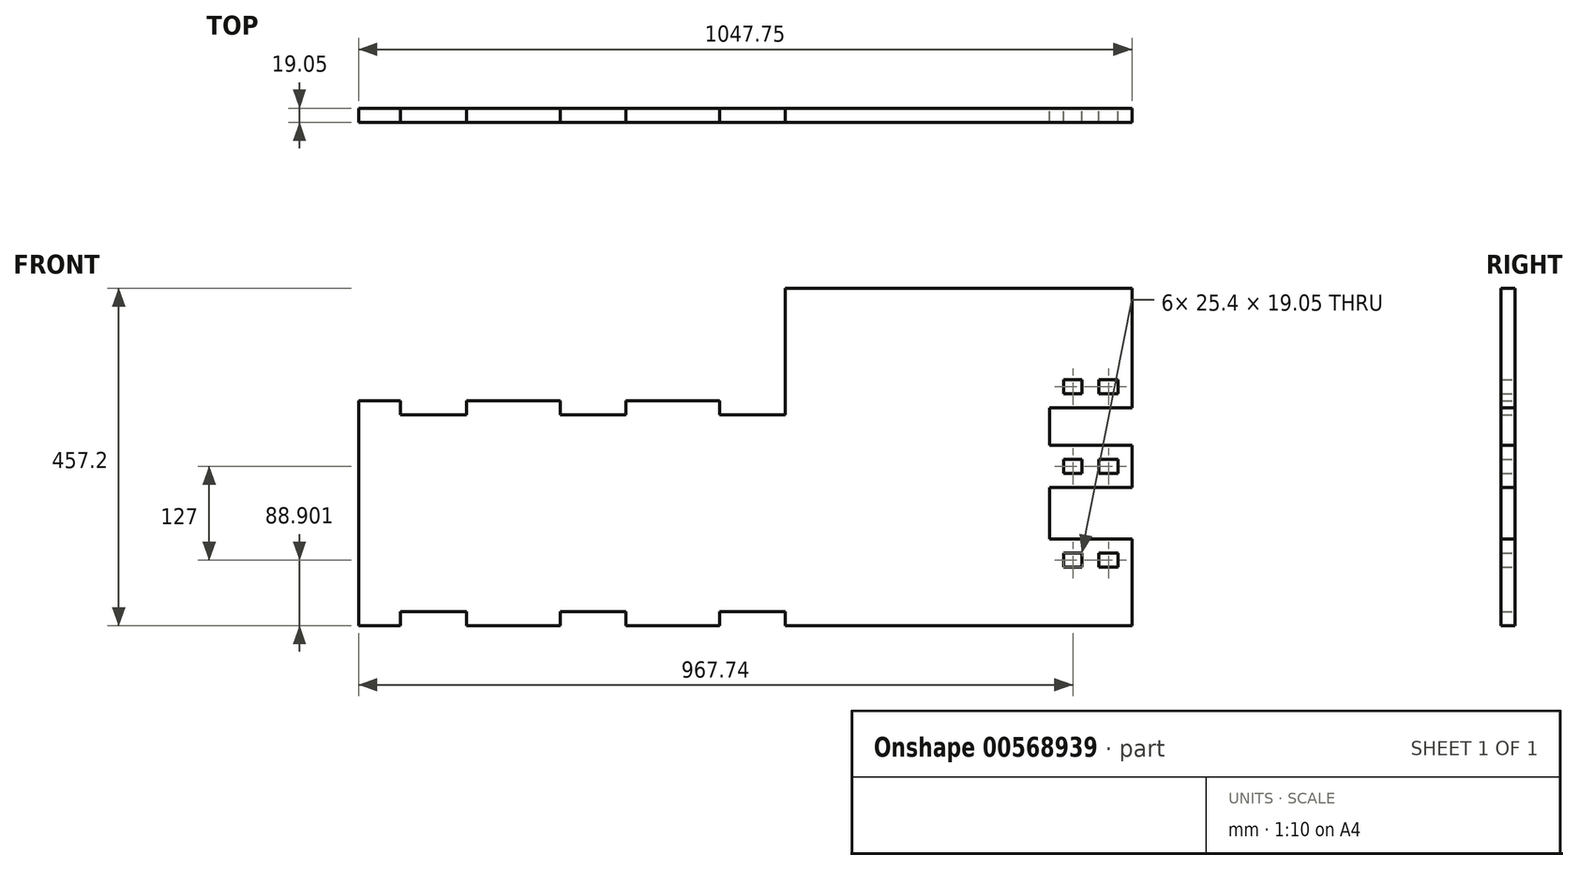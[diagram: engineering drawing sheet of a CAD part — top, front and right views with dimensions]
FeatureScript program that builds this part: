
annotation { "Feature Type Name" : "Feature", "Feature Type Description" : "" }
export const myFeature = defineFeature(function(context is Context, id is Id, definition is map)
    precondition{}
    {
        {
            var Q0;
            Q0=qCreatedBy(makeId("Front.planeOp"),FACE);
            var sketch = newSketch(context, id + "F0", { "sketchPlane" : qUnion([Q0])});
            skLineSegment(sketch, "E0.bottom", {"start": v(-524.7, 138.05) * mm, "end": v(542.1, 138.05) * mm});
            skLineSegment(sketch, "E0.top", {"start": v(-524.7, -166.75) * mm, "end": v(542.1, -166.75) * mm});
            skLineSegment(sketch, "E0.left", {"start": v(-524.7, 138.05) * mm, "end": v(-524.7, -166.75) * mm});
            skLineSegment(sketch, "E1.bottom", {"start": v(-448.5, -166.75) * mm, "end": v(-359.6, -166.75) * mm});
            skLineSegment(sketch, "E1.top", {"start": v(-448.5, -147.7) * mm, "end": v(-359.6, -147.7) * mm});
            skLineSegment(sketch, "E1.left", {"start": v(-448.5, -166.75) * mm, "end": v(-448.5, -147.7) * mm});
            skLineSegment(sketch, "E1.right", {"start": v(-359.6, -166.75) * mm, "end": v(-359.6, -147.7) * mm});
            skLineSegment(sketch, "E2.bottom", {"start": v(-232.6, -166.75) * mm, "end": v(-143.7, -166.75) * mm});
            skLineSegment(sketch, "E2.top", {"start": v(-232.6, -147.7) * mm, "end": v(-143.7, -147.7) * mm});
            skLineSegment(sketch, "E2.left", {"start": v(-232.6, -166.75) * mm, "end": v(-232.6, -147.7) * mm});
            skLineSegment(sketch, "E2.right", {"start": v(-143.7, -166.75) * mm, "end": v(-143.7, -147.7) * mm});
            skLineSegment(sketch, "E3.bottom", {"start": v(-16.7, -166.75) * mm, "end": v(72.2, -166.75) * mm});
            skLineSegment(sketch, "E3.top", {"start": v(-16.7, -147.7) * mm, "end": v(72.2, -147.7) * mm});
            skLineSegment(sketch, "E3.left", {"start": v(-16.7, -166.75) * mm, "end": v(-16.7, -147.7) * mm});
            skLineSegment(sketch, "E3.right", {"start": v(72.2, -166.75) * mm, "end": v(72.2, -147.7) * mm});
            skLineSegment(sketch, "E4.bottom", {"start": v(-524.7, 138.05) * mm, "end": v(-505.64, 138.05) * mm});
            skLineSegment(sketch, "E4.top", {"start": v(-524.7, -166.75) * mm, "end": v(-505.64, -166.75) * mm});
            skLineSegment(sketch, "E4.right", {"start": v(-505.64, 138.05) * mm, "end": v(-505.64, -166.75) * mm});
            skLineSegment(sketch, "E5.bottom", {"start": v(542.1, -49.27) * mm, "end": v(430.35, -49.27) * mm});
            skLineSegment(sketch, "E6", {"start": v(542.1, -166.75) * mm, "end": v(542.1, -49.27) * mm});
            skLineSegment(sketch, "E7.bottom", {"start": v(-448.5, 138.05) * mm, "end": v(-359.6, 138.05) * mm});
            skLineSegment(sketch, "E7.top", {"start": v(-448.5, 119) * mm, "end": v(-359.6, 119) * mm});
            skLineSegment(sketch, "E7.left", {"start": v(-448.5, 138.05) * mm, "end": v(-448.5, 119) * mm});
            skLineSegment(sketch, "E7.right", {"start": v(-359.6, 138.05) * mm, "end": v(-359.6, 119) * mm});
            skLineSegment(sketch, "E8.bottom", {"start": v(-232.6, 138.05) * mm, "end": v(-143.7, 138.05) * mm});
            skLineSegment(sketch, "E8.top", {"start": v(-232.6, 119) * mm, "end": v(-143.7, 119) * mm});
            skLineSegment(sketch, "E8.left", {"start": v(-232.6, 138.05) * mm, "end": v(-232.6, 119) * mm});
            skLineSegment(sketch, "E8.right", {"start": v(-143.7, 138.05) * mm, "end": v(-143.7, 119) * mm});
            skLineSegment(sketch, "E9.bottom", {"start": v(-16.7, 138.05) * mm, "end": v(72.2, 138.05) * mm});
            skLineSegment(sketch, "E9.top", {"start": v(-16.7, 119) * mm, "end": v(72.2, 119) * mm});
            skLineSegment(sketch, "E9.left", {"start": v(-16.7, 138.05) * mm, "end": v(-16.7, 119) * mm});
            skLineSegment(sketch, "E9.right", {"start": v(72.2, 138.05) * mm, "end": v(72.2, 119) * mm});
            skLineSegment(sketch, "E10.bottom", {"start": v(523.06, -49.27) * mm, "end": v(497.66, -49.27) * mm});
            skLineSegment(sketch, "E11.bottom", {"start": v(474.8, -49.27) * mm, "end": v(449.4, -49.27) * mm});
            skLineSegment(sketch, "E12.bottom", {"start": v(542.1, -166.75) * mm, "end": v(72.2, -166.75) * mm});
            skLineSegment(sketch, "E12.top", {"start": v(542.1, -319.15) * mm, "end": v(72.2, -319.15) * mm});
            skLineSegment(sketch, "E12.left", {"start": v(542.1, -166.75) * mm, "end": v(542.1, -319.15) * mm});
            skLineSegment(sketch, "E12.right", {"start": v(72.2, -166.75) * mm, "end": v(72.2, -319.15) * mm});
            skLineSegment(sketch, "E13.bottom", {"start": v(72.2, 138.05) * mm, "end": v(542.1, 138.05) * mm});
            skLineSegment(sketch, "E13.top", {"start": v(72.2, 290.45) * mm, "end": v(542.1, 290.45) * mm});
            skLineSegment(sketch, "E13.left", {"start": v(72.2, 138.05) * mm, "end": v(72.2, 290.45) * mm});
            skLineSegment(sketch, "E13.right", {"start": v(542.1, 138.05) * mm, "end": v(542.1, 290.45) * mm});
            skLineSegment(sketch, "E14", {"start": v(430.35, -49.27) * mm, "end": v(430.35, 128.53) * mm});
            skLineSegment(sketch, "E15", {"start": v(430.35, 128.53) * mm, "end": v(542.1, 128.53) * mm});
            skLineSegment(sketch, "E16", {"start": v(542.1, 138.05) * mm, "end": v(542.1, 128.53) * mm});
            skLineSegment(sketch, "E17.bottom", {"start": v(449.4, 128.53) * mm, "end": v(474.8, 128.53) * mm});
            skLineSegment(sketch, "E17.top", {"start": v(449.4, 138.05) * mm, "end": v(474.8, 138.05) * mm});
            skLineSegment(sketch, "E18.bottom", {"start": v(497.66, 128.53) * mm, "end": v(523.06, 128.53) * mm});
            skLineSegment(sketch, "E19.right", {"start": v(430.35, -49.27) * mm, "end": v(430.35, -23.87) * mm});
            skLineSegment(sketch, "E20.bottom", {"start": v(542.1, 128.53) * mm, "end": v(430.35, 128.53) * mm});
            skLineSegment(sketch, "E20.right", {"start": v(430.35, 128.53) * mm, "end": v(430.35, 90.43) * mm});
            skLineSegment(sketch, "E21.bottom", {"start": v(430.35, 77.73) * mm, "end": v(542.1, 77.73) * mm});
            skLineSegment(sketch, "E21.top", {"start": v(430.35, 20.58) * mm, "end": v(542.1, 20.58) * mm});
            skLineSegment(sketch, "E21.left", {"start": v(430.35, 77.73) * mm, "end": v(430.35, 20.58) * mm});
            skLineSegment(sketch, "E21.right", {"start": v(542.1, 77.73) * mm, "end": v(542.1, 20.58) * mm});
            skLineSegment(sketch, "E22", {"start": v(449.4, 58.68) * mm, "end": v(474.8, 58.68) * mm});
            skLineSegment(sketch, "E23", {"start": v(449.4, 39.63) * mm, "end": v(474.8, 39.63) * mm});
            skLineSegment(sketch, "E24", {"start": v(497.66, 58.68) * mm, "end": v(523.06, 58.68) * mm});
            skLineSegment(sketch, "E25", {"start": v(497.66, 39.63) * mm, "end": v(523.06, 39.63) * mm});
            skLineSegment(sketch, "E26", {"start": v(523.06, 39.63) * mm, "end": v(523.06, 58.68) * mm});
            skLineSegment(sketch, "E27", {"start": v(497.66, 58.68) * mm, "end": v(497.66, 39.63) * mm});
            skLineSegment(sketch, "E28", {"start": v(449.4, 58.68) * mm, "end": v(449.4, 39.63) * mm});
            skLineSegment(sketch, "E29", {"start": v(474.8, 58.68) * mm, "end": v(474.8, 39.63) * mm});
            skLineSegment(sketch, "E30.bottom", {"start": v(449.4, 147.58) * mm, "end": v(474.8, 147.58) * mm});
            skLineSegment(sketch, "E30.top", {"start": v(449.4, 166.63) * mm, "end": v(474.8, 166.63) * mm});
            skLineSegment(sketch, "E30.left", {"start": v(449.4, 147.58) * mm, "end": v(449.4, 166.63) * mm});
            skLineSegment(sketch, "E30.right", {"start": v(474.8, 147.58) * mm, "end": v(474.8, 166.63) * mm});
            skLineSegment(sketch, "E31.bottom", {"start": v(497.66, 166.63) * mm, "end": v(523.06, 166.63) * mm});
            skLineSegment(sketch, "E31.top", {"start": v(497.66, 147.58) * mm, "end": v(523.06, 147.58) * mm});
            skLineSegment(sketch, "E31.left", {"start": v(497.66, 166.63) * mm, "end": v(497.66, 147.58) * mm});
            skLineSegment(sketch, "E31.right", {"start": v(523.06, 166.63) * mm, "end": v(523.06, 147.58) * mm});
            skLineSegment(sketch, "E32.bottom", {"start": v(449.4, -68.32) * mm, "end": v(474.8, -68.32) * mm});
            skLineSegment(sketch, "E32.top", {"start": v(449.4, -87.37) * mm, "end": v(474.8, -87.37) * mm});
            skLineSegment(sketch, "E32.left", {"start": v(449.4, -68.32) * mm, "end": v(449.4, -87.37) * mm});
            skLineSegment(sketch, "E32.right", {"start": v(474.8, -68.32) * mm, "end": v(474.8, -87.37) * mm});
            skLineSegment(sketch, "E33.bottom", {"start": v(497.66, -68.32) * mm, "end": v(523.06, -68.32) * mm});
            skLineSegment(sketch, "E33.top", {"start": v(497.66, -87.37) * mm, "end": v(523.06, -87.37) * mm});
            skLineSegment(sketch, "E33.left", {"start": v(497.66, -68.32) * mm, "end": v(497.66, -87.37) * mm});
            skLineSegment(sketch, "E33.right", {"start": v(523.06, -68.32) * mm, "end": v(523.06, -87.37) * mm});
            skLineSegment(sketch, "E34", {"start": v(-524.7, -14.35) * mm, "end": v(1042.2, -14.35) * mm, "construction": true});
            skSolve(sketch);
        }
        {
            var Q0;
            Q0=makeQuery(id+"F0.imprint","IMPRINT",FACE,{"disambiguationData":[TD([[makeQuery(id+"F0.imprint","IMPRINT",EDGE,{"derivedFrom":sQuery(id+"F0.wireOp",EDGE,"E0.bottom")}),-1.0]])]});
            var Q1;
            {var subQ14=sQuery(id+"F0.wireOp",EDGE,"4piZZYSk-cvEN-wXRT-BMMY-i1fo28OA3dKF.top");Q1=makeQuery(id+"F0.imprint","IMPRINT",FACE,{"disambiguationData":[TD([[makeQuery(id+"F0.imprint","IMPRINT",EDGE,{"derivedFrom":subQ14}),1.0]])]});}
            var Q2;
            Q2=makeQuery(id+"F0.imprint","IMPRINT",FACE,{"disambiguationData":[TD([[makeQuery(id+"F0.imprint","IMPRINT",EDGE,{"derivedFrom":sQuery(id+"F0.wireOp",EDGE,"E12.bottom")}),1.0]])]});
            var Q3;
            {var subQ0=sQuery(id+"F0.wireOp",EDGE,"BTT1ppKT-5z5v-0DyU-JSBF-GySog7vsvcC7.left");Q3=makeQuery(id+"F0.imprint","IMPRINT",FACE,{"disambiguationData":[TD([[makeQuery(id+"F0.imprint","IMPRINT",EDGE,{"derivedFrom":subQ0}),-1.0]])]});}
            var Q4;
            {var subQ0=sQuery(id+"F0.wireOp",EDGE,"4piZZYSk-cvEN-wXRT-BMMY-i1fo28OA3dKF.right");var subQ5=sQuery(id+"F0.wireOp",EDGE,"E13.bottom");var subQ7=makeQuery(id+"F0.imprint","INTERSECT",VERTEX,{"derivedFrom":[subQ0,subQ5]});Q4=makeQuery(id+"F0.imprint","IMPRINT",FACE,{"disambiguationData":[TD([[makeQuery(id+"F0.imprint","IMPRINT",EDGE,{"disambiguationData":[TD([[subQ7,-1.0]])],"derivedFrom":subQ5}),-1.0]])]});}
            var Q5;
            Q5=makeQuery(id+"F0.imprint","IMPRINT",FACE,{"disambiguationData":[TD([[makeQuery(id+"F0.imprint","IMPRINT",EDGE,{"derivedFrom":sQuery(id+"F0.wireOp",EDGE,"E13.top")}),-1.0]])]});
            var Q6;
            Q6=makeQuery(id+"F0.imprint","IMPRINT",FACE,{"disambiguationData":[TD([[makeQuery(id+"F0.imprint","IMPRINT",EDGE,{"derivedFrom":sQuery(id+"F0.wireOp",EDGE,"E19.top")}),1.0]])]});
            var Q7;
            Q7=makeQuery(id+"F0.imprint","IMPRINT",FACE,{"disambiguationData":[TD([[makeQuery(id+"F0.imprint","IMPRINT",EDGE,{"derivedFrom":sQuery(id+"F0.wireOp",EDGE,"E20.top")}),-1.0]])]});
            var Q8;
            Q8=makeQuery(id+"F0.imprint","IMPRINT",FACE,{"disambiguationData":[TD([[makeQuery(id+"F0.imprint","IMPRINT",EDGE,{"derivedFrom":sQuery(id+"F0.wireOp",EDGE,"E21.bottom")}),-1.0]])]});
            extrude(context, id + "F1", {"entities" : qUnion([Q0, Q1, Q2, Q3, Q4, Q5, Q6, Q7, Q8]), "depth" : 19.05 * mm, "offsetDistance" : 25.4 * mm});
        }
    });
